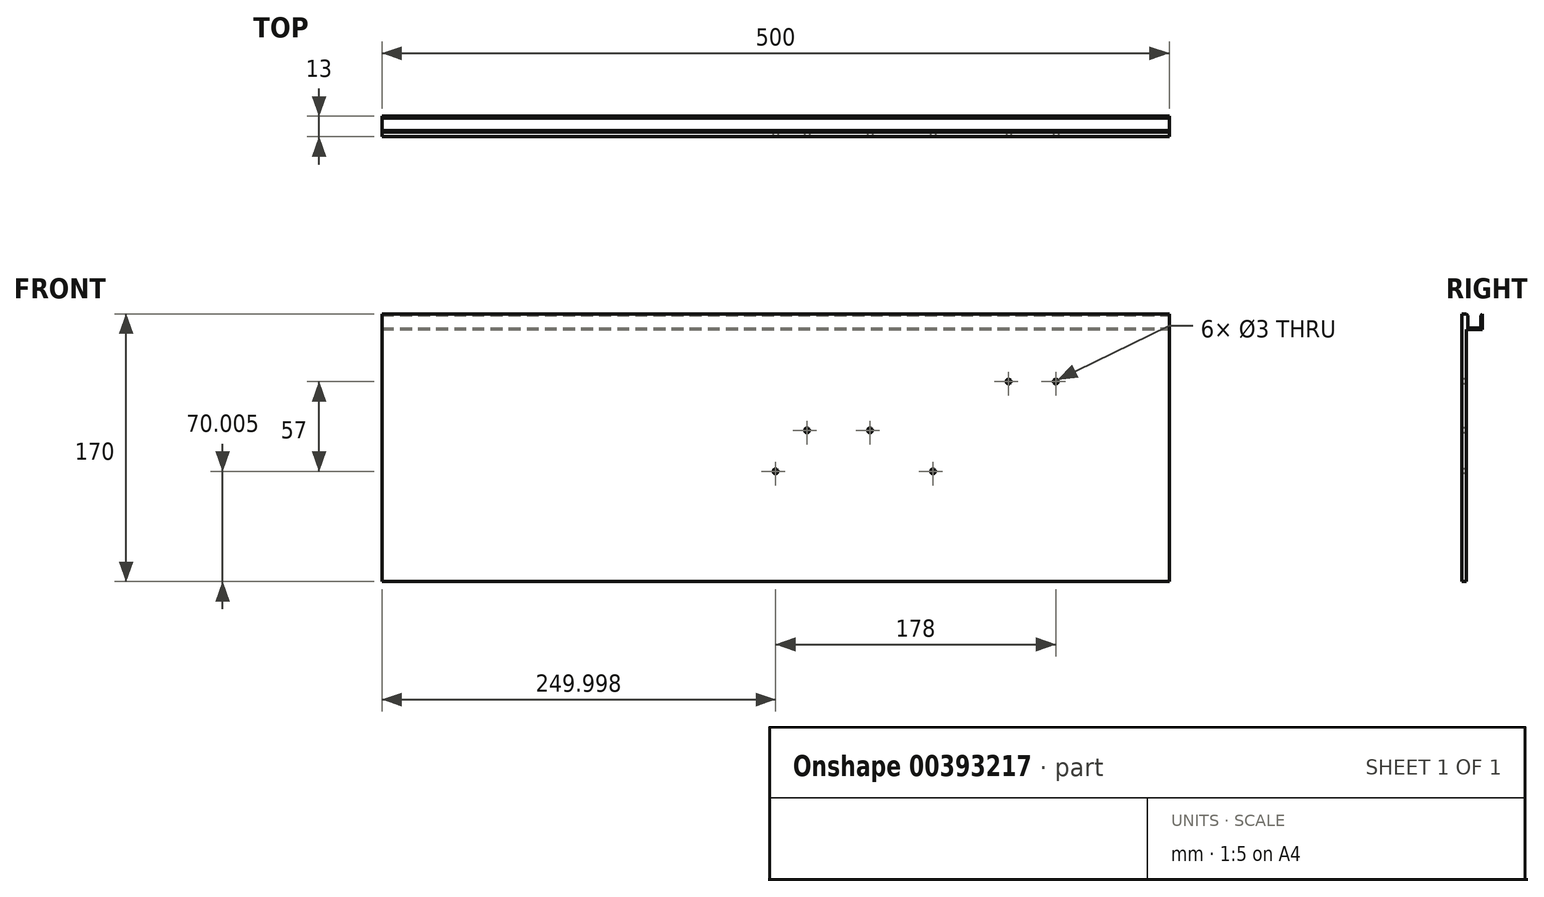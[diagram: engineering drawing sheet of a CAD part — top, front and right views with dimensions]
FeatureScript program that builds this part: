
annotation { "Feature Type Name" : "Feature", "Feature Type Description" : "" }
export const myFeature = defineFeature(function(context is Context, id is Id, definition is map)
    precondition{}
    {
        {
            var Q0;
            Q0=qCreatedBy(makeId("Front.planeOp"),FACE);
            var sketch = newSketch(context, id + "F0", { "sketchPlane" : qUnion([Q0])});
            skLineSegment(sketch, "E0.bottom", {"start": v(-188.98, -72) * mm, "end": v(311.02, -72) * mm});
            skLineSegment(sketch, "E0.top", {"start": v(-188.98, 98) * mm, "end": v(311.02, 98) * mm});
            skLineSegment(sketch, "E0.left", {"start": v(-188.98, -72) * mm, "end": v(-188.98, 98) * mm});
            skLineSegment(sketch, "E0.right", {"start": v(311.02, -72) * mm, "end": v(311.02, 98) * mm});
            skSolve(sketch);
        }
        {
            var Q0;
            Q0 = qSketchRegion(id + "F0", true);
            extrude(context, id + "F1", {"entities" : qUnion([Q0]), "depth" : 3 * mm});
        }
        {
            var Q0;
            Q0=makeQuery(id+"F1.opExtrude","SWEPT_FACE",FACE,{"disambiguationData":[OSD([sQuery(id+"F0.wireOp",EDGE,"E0.right")])]});
            var sketch = newSketch(context, id + "F2", { "sketchPlane" : qUnion([Q0])});
            skLineSegment(sketch, "E1.top", {"start": v(0, 88) * mm, "end": v(10, 88) * mm});
            skLineSegment(sketch, "E1.left", {"start": v(0, 98) * mm, "end": v(0, 88) * mm});
            skLineSegment(sketch, "E1.right", {"start": v(10, 98) * mm, "end": v(10, 88) * mm});
            skLineSegment(sketch, "E2", {"start": v(1, 89) * mm, "end": v(9, 89) * mm});
            skLineSegment(sketch, "E3", {"start": v(1, 97) * mm, "end": v(0, 98) * mm});
            skLineSegment(sketch, "E4", {"start": v(9, 97) * mm, "end": v(10, 98) * mm});
            skLineSegment(sketch, "E5", {"start": v(1, 97) * mm, "end": v(1, 89) * mm});
            skLineSegment(sketch, "E6", {"start": v(9, 89) * mm, "end": v(9, 97) * mm});
            skSolve(sketch);
        }
        {
            var Q0;
            Q0 = qSketchRegion(id + "F2", true);
            var Q1;
            Q1=makeQuery(id+"F1.opExtrude","SWEPT_FACE",FACE,{"disambiguationData":[OSD([sQuery(id+"F0.wireOp",EDGE,"E0.left")])]});
            extrude(context, id + "F3", {"entities" : qUnion([Q0]), "operationType" : NewBodyOperationType.ADD, "endBound" : BoundingType.UP_TO_SURFACE, "oppositeDirection" : true, "endBoundEntityFace" : qUnion([Q1]), "depth" : 25 * mm});
        }
        {
            var Q0;
            Q0=makeQuery(id+"F1.opExtrude","CAP_FACE",FACE,{"disambiguationData":[OSD([sQuery(id+"F0.wireOp",EDGE,"E0.bottom"),sQuery(id+"F0.wireOp",EDGE,"E0.top"),sQuery(id+"F0.wireOp",EDGE,"E0.left"),sQuery(id+"F0.wireOp",EDGE,"E0.right")])],"isStart":false});
            var sketch = newSketch(context, id + "F4", { "sketchPlane" : qUnion([Q0])});
            skPoint(sketch, "E7", {"position": v(61.02, -2) * mm});
            skPoint(sketch, "E8", {"position": v(161.02, -2) * mm});
            skPoint(sketch, "E9", {"position": v(209.02, 55) * mm});
            skPoint(sketch, "E10", {"position": v(239.02, 55) * mm});
            skPoint(sketch, "E11", {"position": v(81.02, 24) * mm});
            skPoint(sketch, "E12", {"position": v(121.02, 24) * mm});
            skSolve(sketch);
        }
        {
            var Q0;
            Q0=sQuery(id+"F4.wireOp",VERTEX,"E7");
            var Q1;
            Q1=sQuery(id+"F4.wireOp",VERTEX,"E11");
            var Q2;
            Q2=sQuery(id+"F4.wireOp",VERTEX,"E12");
            var Q3;
            Q3=sQuery(id+"F4.wireOp",VERTEX,"E8");
            var Q4;
            Q4=sQuery(id+"F4.wireOp",VERTEX,"E9");
            var Q5;
            Q5=sQuery(id+"F4.wireOp",VERTEX,"E10");
            var Q6;
            Q6=makeQuery(id+"F1.opExtrude","SWEPT_BODY",BODY,{"disambiguationData":[OSD([sQuery(id+"F0.wireOp",EDGE,"E0.bottom"),sQuery(id+"F0.wireOp",EDGE,"E0.top"),sQuery(id+"F0.wireOp",EDGE,"E0.left"),sQuery(id+"F0.wireOp",EDGE,"E0.right")])]});
            hole(context, id + "F5", {"style" : HoleStyle.SIMPLE, "endStyle" : HoleEndStyle.BLIND, "holeDiameter" : 3 * mm, "holeDepth" : 25 * mm, "isTappedThrough" : true, "tappedDepth" : 12 * mm, "tapClearance" : 3, "locations" : qUnion([Q0, Q1, Q2, Q3, Q4, Q5]), "scope" : qUnion([Q6])});
        }
    });
